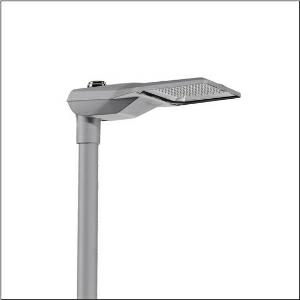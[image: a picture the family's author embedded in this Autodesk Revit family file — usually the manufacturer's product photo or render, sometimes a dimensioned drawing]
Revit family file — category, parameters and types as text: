
# Revit family: streetlight_sl_21_midi___p0_8a_5xe7u67n08mb_9091
name_source: partatom
category: Lighting Fixtures
units: mm (PartAtom-declared; Revit-internal decimal feet)

## family parameters
Cut with Voids When Loaded = No
Host = Face
Light Source = No
Part Type = Normal
Room Calculation Point = No
Round Connector Dimension = Use Diameter
Shared = No

## types (1)
- --- (1 x LED, 16380 lm, 134.3 W, 2700K)
    Apparent Load = 134 VA
    CIE Flux Codes = 33 69 96 100 100
    Color Rendering = 70
    Color Temperature = 2700K
    Default Elevation = 1800 mm
    Description = Streetlight SL 21 midi, mast luminaire, primary light control with lens, of PMMA, primary optical cover: cover, of toughened safety glass, transparent, light distribution: P0.8a, light emission: direct distribution, primary light characteristic: asymmetric, installation type: side-entry, LED, 3G 2.5mm², High Power LED, rated luminous flux: 16.380lm, luminous efficacy: 122lm/W, light colour: 727, colour temperature: 2700K, control gear: NEMA (7pin), control: flexible luminous flux parameterisation, time-dependent luminous flux control, constant luminous flux control, pre-setting: linear dimming characteristic, overheat protection, mains connection: 220..240V, AC, 50/60Hz, connection cable pre-assembled, cable length: 12,5m, wiring characteristics: H05VV-F, start of lifetime: 134W, end of service life: 141W, reduction: 60W, luminaire housing, of diecast aluminium (EN AC-44300), powder-coated, SITECO metallic grey (DB 702S), corrosivity category C5 high according to DIN EN ISO 12944, multi-level sealing system, sealing non-destructively replaceable, inclination adjustable: 0°, 5°, 10°, 15°, length: 644mm, width: 335mm, height: 110mm, spigot size: 42mm (side-entry), mounting height: 4..8m, protection rating (complete): IP66, insulation class (complete): insulation class I (protective earthing), certification: CE, ENEC, ENEC+, VDE, impact resistance: IK10, permissible operating ambient temperature for outdoor applications: -40..+50°C, standard-compliant lighting for roads and squares, packaging unit: 1 piece

Light Distribution: P0.8a
    Height = 111 mm
    Lamp = 1 x LED
    Lamp Light Flux = 16380 lm
    Lamp Power = 134.3 W
    Lamp count = 1
    Length = 644 mm
    Luminous efficacy = 122 lm/W
    Manufacturer = Siteco
    ModVariant = No
    Model = 5XE7U67N08MB
    Number of Poles = 1
    OnlyDefault = Yes
    Power Factor = 1
    Product Name = Streetlight SL 21 midi | P0.8a
    Product group = mast luminaire | pylon top
    ProductGroupID = 6100
    Protection Class = Protection class I
    Protection Degree = IP 66
    RLX_Detail_Level = 1
    RLX_Emergency_Light_Flux = 0 lm
    RLX_Emergency_Type = 0
    RLX_Emergency_Type_DB = No
    RlxData = <blob elided: 89997 chars, md5=83d790ea>
    Socket = socket
    Standby Power = 0 W
    System Light Flux = 16381 lm
    System Power = 134 W
    Type Comments = factory setting: luminous flux: 100 % | dim-lin: 254 | 687 mA
    Type Image = l_1294377.jpg
    URL = http://relux.com
    VarID = @adj_080893
    Voltage = 0 V
    Weight = 0.00 kg
    Width = 336 mm

## geometry (parser evidence)
native form markers: Blend x4, Sweep x9
no freeform markers — native parametric forms only
